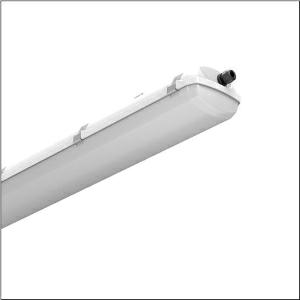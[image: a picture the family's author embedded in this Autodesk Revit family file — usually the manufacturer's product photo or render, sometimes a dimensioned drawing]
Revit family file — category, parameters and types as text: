
# Revit family: monsun_r__ex_51fxb2dl440a_885d
name_source: partatom
category: Lighting Fixtures
units: mm (PartAtom-declared; Revit-internal decimal feet)

## family parameters
Cut with Voids When Loaded = No
Host = Face
Light Source = No
Part Type = Normal
Room Calculation Point = No
Round Connector Dimension = Use Diameter
Shared = No

## types (1)
- Monsun® Ex (1 x LED, 4500 lm, 29.2 W, 4000K)
    Apparent Load = 29 VA
    CIE Flux Codes = 43 73 91 93 100
    Color Rendering = 80
    Color Temperature = 4000K
    Default Elevation = 1800 mm
    Description = Monsun® Ex, damp-proof luminaire, primary optical cover: cover, of PC, UV-stabilised, opal, light emission: direct distribution, primary light characteristic: symmetric, installation type: surface-mounted, LED, rated luminous flux: 4.500lm, luminous efficacy: 154lm/W, light colour: 840, colour temperature: 4000K, control gear: ECG DALI, with terminal, 5-pole, max. 2.5mm², through-wiring: 7x 2.5mm², mains connection: 220..240V, AC, 50/60Hz, rated input power: 29W, housing, of PC, light grey (RAL 7035), incl. blind plug, incl. 1x Ex cable gland M20 for cable diameter 7..12mm with sealing, length: 1.280mm, width: 155mm, height: 105mm, clip for enclosure, of stainless steel, protection rating (complete): IP66, insulation class (complete): insulation class I (protective earthing), certification: CE, explosion class: zone2,22 II 3G Ex nR IIC T6 GC, II 3D Ex tc IIIC T80°C Dc, impact resistance: IK10, permissible operating ambient temperature: -20..+60°C, LABS conformity tested according to VDMA 24364:2018-05, contact your sales advisor before using the luminaires in applications with unclear chemical exposure, large temperature fluctuations or condensation-forming humidity, packaging unit: 1 piece
    Height = 105 mm
    Lamp = 1 x LED
    Lamp Light Flux = 4500 lm
    Lamp Power = 29.2 W
    Lamp count = 1
    Length = 1280 mm
    Luminous efficacy = 154 lm/W
    Manufacturer = Siteco
    ModVariant = No
    Model = 51FXB2DL440A
    Mounting Place = Ceiling
    Mounting Type = Surface mounted
    Number of Poles = 1
    OnlyDefault = Yes
    Power Factor = 1
    Product Name = Monsun® Ex
    Product group = damp-proof luminaire
    ProductGroupID = 301
    Protection Class = Protection class I
    Protection Degree = IP 66
    RLX_Detail_Level = 1
    RLX_Emergency_Light_Flux = 0 lm
    RLX_Emergency_Type = 0
    RLX_Emergency_Type_DB = No
    RlxData = <blob elided: 41653 chars, md5=a1b8b685>
    Socket = socket
    Standby Power = 0 W
    System Light Flux = 4500 lm
    System Power = 29 W
    Type Comments = Product without accessories
    Type Image = l_1258882.jpg
    URL = http://relux.com
    VarID = ---
    Voltage = 0 V
    Weight = 0.00 kg
    Width = 155 mm

## geometry (parser evidence)
native form markers: Blend x4, Sweep x11
no freeform markers — native parametric forms only
